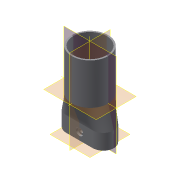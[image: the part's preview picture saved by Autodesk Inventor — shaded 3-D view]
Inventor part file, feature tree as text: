
AUTODESK INVENTOR PART (.ipt)
format: ipt  version: 2015 SP2 (Build 190223200, 223)  size: 285,696 bytes
history: native  units: mm
features: sketch x9, extrude x7, plane x2, mirror x2, projected_geometry x2, other x1, loft x1
ambient origin geometry x8: Origin, YZ Plane, XZ Plane, XY Plane, X Axis, Y Axis, Z Axis, Center Point
bodies: Body1 (feature_tree)
feature tree (24):
  other  "Sólido1"
  extrude  "Extrusión1"  Depth=32.5mm
  plane  "Plano de trabajo1"
  extrude  "Extrusión2"  [1 undecoded]
  extrude  "Extrusión3"  Depth=20.5mm
  loft  "Solevación1"
  mirror  "Simetría1"
  mirror  "Simetría2"
  extrude  "Extrusión4"  Depth=15.0mm TaperAngle=0.0deg
  extrude  "Extrusión5"  Depth=16.0mm
  extrude  "Extrusión6"  Depth=2.0mm
  extrude  "Extrusión7"  TaperAngle=0.0deg  [1 undecoded]
  sketch  "Boceto1"  dims[d0=35.5mm d1=32.5mm]
  sketch  "Boceto2"  dims[d2=40.0mm d3=0.0mm d4=-35.0mm]
  sketch  "Boceto3"  dims[d5=26.0mm d6=20.5mm]
  sketch  "Boceto4"  dims[d7=26.0mm d8=26.0mm]
  sketch  "Boceto5"  dims[d9=13.0mm d10=15.0mm d11=0.0mm]
  projected_geometry  "Contorno proyectado1"
  plane  "Plano de trabajo2"
  sketch  "Boceto6"  dims[d12=16.0mm d13=16.0mm]
  sketch  "Boceto7"  dims[d14=15.0mm d15=0.0mm d16=2.0mm]
  projected_geometry  "Contorno proyectado2"
  sketch  "Boceto8"  dims[d17=2.0mm d18=0.0mm d19=90.0deg]
  sketch  "Boceto9"  dims[d20=0.0mm d21=90.0deg d22=3.0mm d23=14.0mm d24=20.0mm d25=0.0mm d26=7.2mm d27=2.0mm d28=0.0mm d29=3.75mm d30=2.0mm d31=0.0mm d32=6.41mm d33=5.25mm d34=0.0mm]
note: 2 required parameter values undecoded (feature->parameter linkage not recoverable at this tier; creation-order binding heuristic only, values carry confidence <= 0.55)
